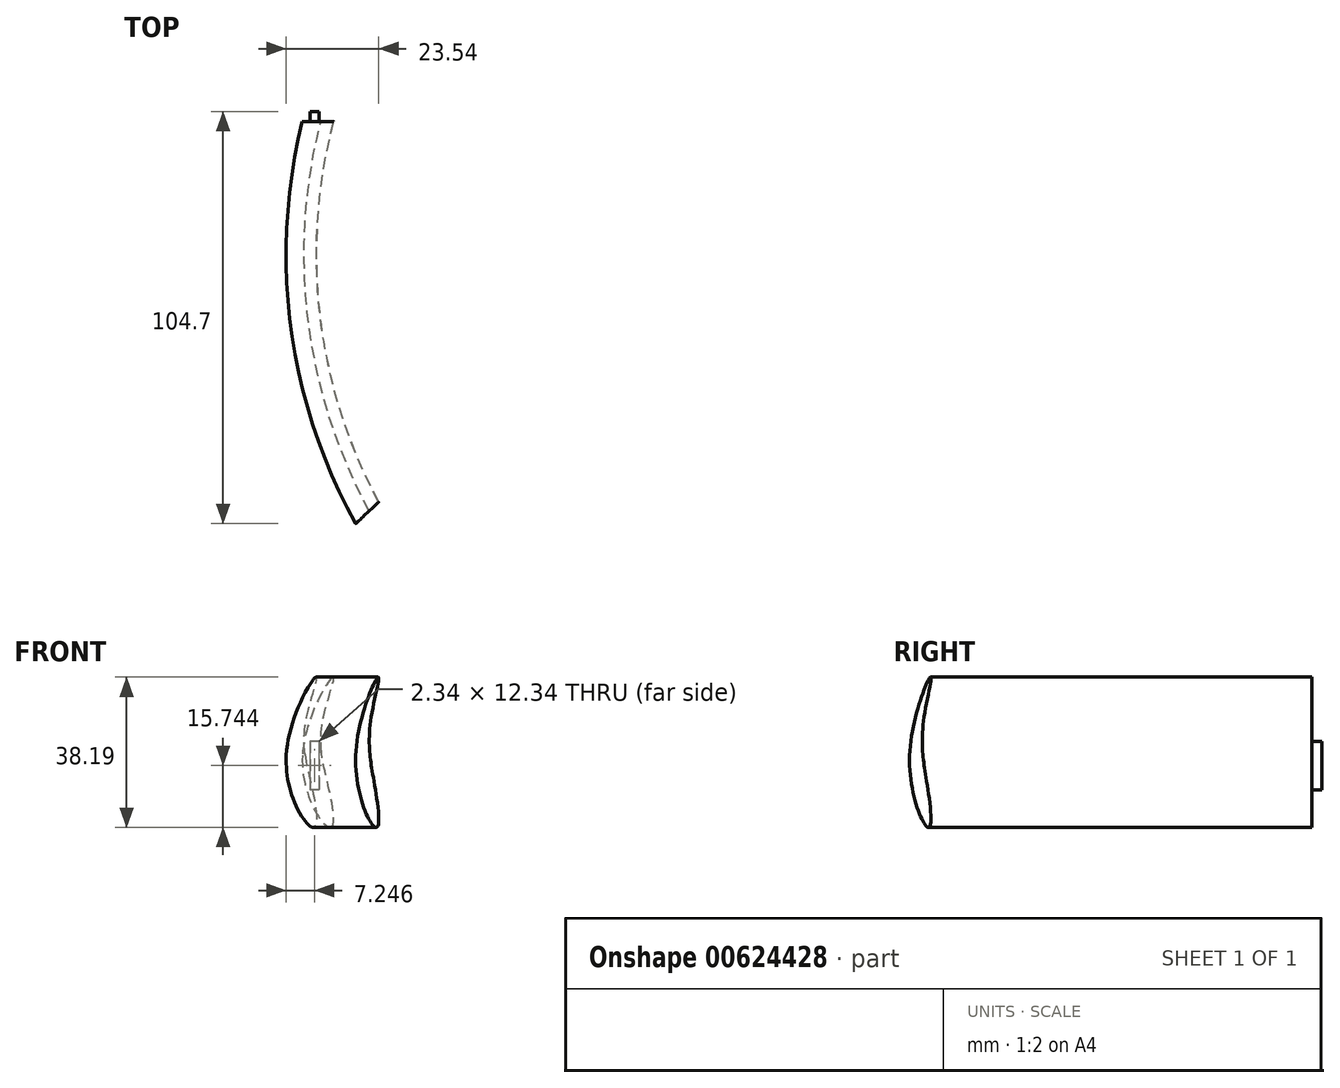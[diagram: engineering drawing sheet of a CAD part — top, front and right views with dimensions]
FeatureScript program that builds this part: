
annotation { "Feature Type Name" : "Feature", "Feature Type Description" : "" }
export const myFeature = defineFeature(function(context is Context, id is Id, definition is map)
    precondition{}
    {
        {
            var Q0;
            Q0=qCreatedBy(makeId("Front.planeOp"),FACE);
            var sketch = newSketch(context, id + "F0", { "sketchPlane" : qUnion([Q0])});
            skFitSpline(sketch, "E0.MirrorC", {"points": [v(4.82, 20.35) * mm, v(-3.03, 0.4) * mm, v(3.62, -17.75) * mm, v(4.82, -16.98) * mm, v(3.23, -5.82) * mm, v(1.88, 0.74) * mm, v(2.46, 10.73) * mm, v(4.82, 20.35) * mm]});
            skLineSegment(sketch, "E1.MirrorCS", {"start": v(1.88, 0.74) * mm, "end": v(-3.03, 0.4) * mm});
            skSolve(sketch);
        }
        {
            var Q0;
            Q0=qCreatedBy(makeId("Top.planeOp"),FACE);
            var sketch = newSketch(context, id + "F1", { "sketchPlane" : qUnion([Q0])});
            skLineSegment(sketch, "E2", {"start": v(0, 0) * mm, "end": v(0, -100.08) * mm});
            skArc(sketch, "E3", {"start": v(-17.95, -100.08) * mm, "mid": v(1.63, -51.94) * mm, "end": v(0, 0) * mm});
            skArc(sketch, "E4", {"start": v(0, 0) * mm, "mid": v(-3.08, -51.24) * mm, "end": v(12.74, -100.08) * mm});
            skSolve(sketch);
        }
        {
            var Q0;
            {var subQ0=sQuery(id+"F0.wireOp",EDGE,"E1.MirrorCS");Q0=makeQuery(id+"F0.imprint","IMPRINT",FACE,{"disambiguationData":[TD([[makeQuery(id+"F0.imprint","IMPRINT",EDGE,{"derivedFrom":subQ0}),-1.0]])]});}
            var Q1;
            {var subQ0=sQuery(id+"F0.wireOp",EDGE,"E1.MirrorCS");Q1=makeQuery(id+"F0.imprint","IMPRINT",FACE,{"disambiguationData":[TD([[makeQuery(id+"F0.imprint","IMPRINT",EDGE,{"derivedFrom":subQ0}),1.0]])]});}
            var Q2;
            Q2=sQuery(id+"F1.wireOp",EDGE,"E4");
            sweep(context, id + "F2", {"profiles" : qUnion([Q0, Q1]), "path" : qUnion([Q2])});
        }
        {
            var Q0;
            Q0=makeQuery(id+"F2.opSweep","CAP_FACE",FACE,{"disambiguationData":[OSD([sQuery(id+"F0.wireOp",EDGE,"E0.MirrorC"),sQuery(id+"F1.wireOp",VERTEX,"E4.start")])],"isStart":true});
            var sketch = newSketch(context, id + "F3", { "sketchPlane" : qUnion([Q0])});
            skLineSegment(sketch, "E5.bottom", {"start": v(-1.24, 4.08) * mm, "end": v(1.1, 4.08) * mm});
            skLineSegment(sketch, "E5.top", {"start": v(-1.24, -8.27) * mm, "end": v(1.1, -8.27) * mm});
            skLineSegment(sketch, "E5.left", {"start": v(-1.24, 4.08) * mm, "end": v(-1.24, -8.27) * mm});
            skLineSegment(sketch, "E5.right", {"start": v(1.1, 4.08) * mm, "end": v(1.1, -8.27) * mm});
            skSolve(sketch);
        }
        {
            var Q0;
            Q0=makeQuery(id+"F3.imprint","IMPRINT",FACE,{"disambiguationData":[TD([[makeQuery(id+"F3.imprint","IMPRINT",EDGE,{"derivedFrom":sQuery(id+"F3.wireOp",EDGE,"E5.bottom")}),-1.0]])]});
            extrude(context, id + "F4", {"entities" : qUnion([Q0]), "operationType" : NewBodyOperationType.ADD, "depth" : 2.54 * mm, "offsetDistance" : 25.4 * mm});
        }
        {
            var Q0;
            Q0=makeQuery(id+"F2.opSweep","SWEPT_BODY",BODY,{"disambiguationData":[OSD([sQuery(id+"F0.wireOp",EDGE,"E0.MirrorC"),sQuery(id+"F1.wireOp",EDGE,"E4")])]});
            transform(context, id + "F5", {"entities" : qUnion([Q0]), "transformType" : TransformType.TRANSLATION_3D, "dx" : 0 * mm, "dy" : 0 * mm, "dz" : 0 * mm, "makeCopy" : true});
        }
    });
